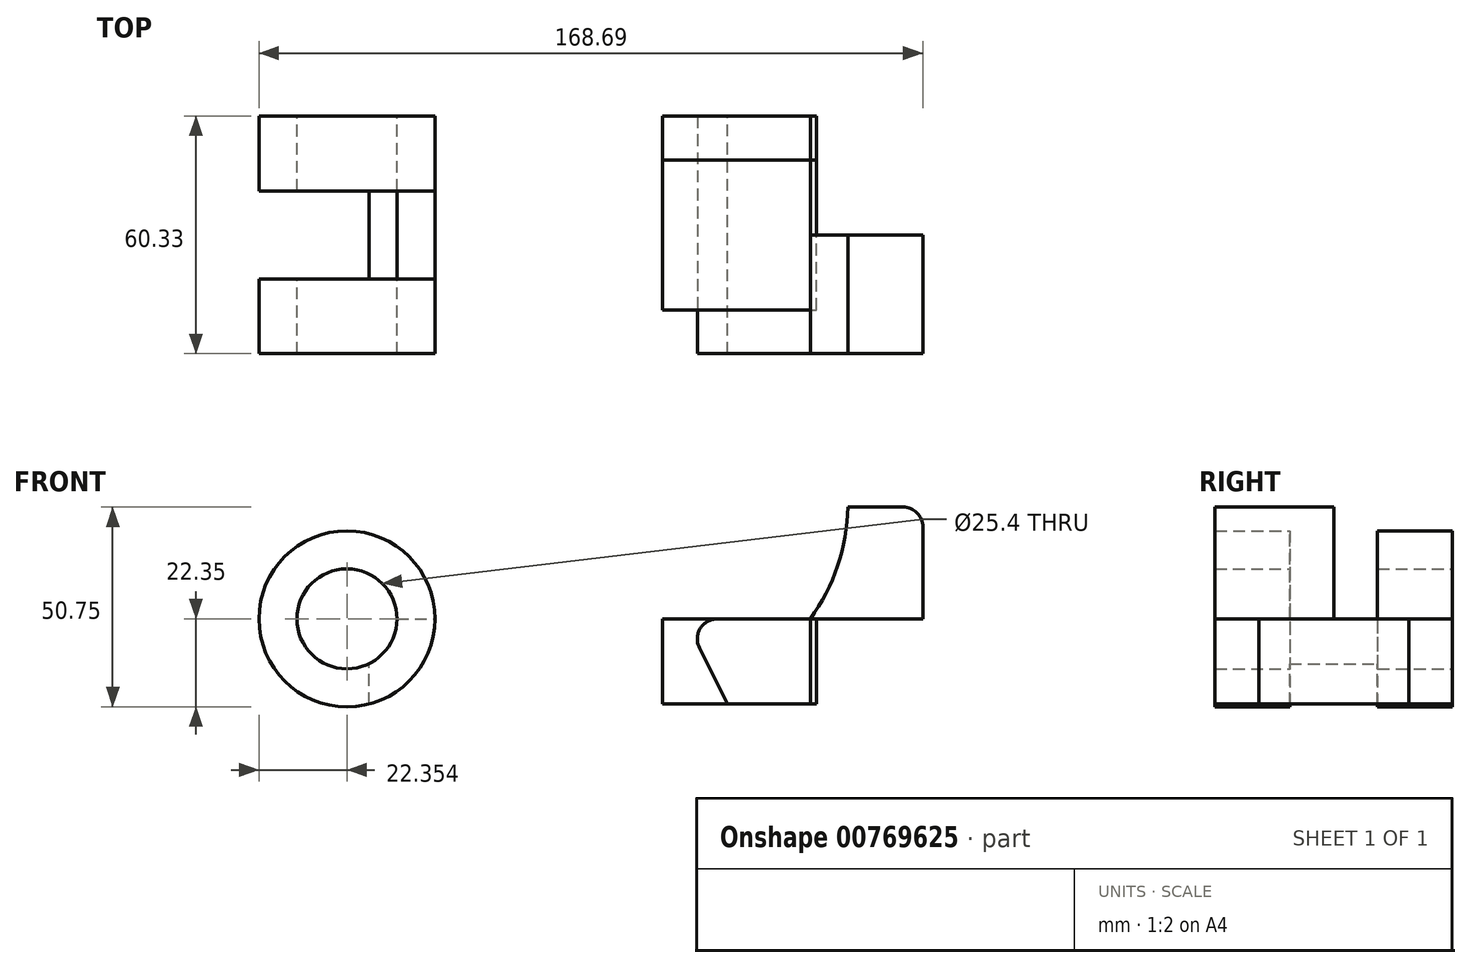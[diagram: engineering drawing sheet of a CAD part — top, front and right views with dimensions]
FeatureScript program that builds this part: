
annotation { "Feature Type Name" : "Feature", "Feature Type Description" : "" }
export const myFeature = defineFeature(function(context is Context, id is Id, definition is map)
    precondition{}
    {
        {
            var Q0;
            Q0=qCreatedBy(makeId("Front.planeOp"),FACE);
            var sketch = newSketch(context, id + "F0", { "sketchPlane" : qUnion([Q0])});
            skPoint(sketch, "E0.middle", {"position": v(114.94, 0) * mm});
            skCircle(sketch, "E1", {"center": v(12.24, 0) * mm, "radius": 12.7 * mm});
            skCircle(sketch, "E2", {"center": v(12.24, 0) * mm, "radius": 22.35 * mm});
            skPoint(sketch, "E3.orphan", {"position": v(17.84, -11.18) * mm});
            skPoint(sketch, "E0.bottom.end.orphan", {"position": v(6.65, 11.18) * mm});
            skPoint(sketch, "E0.left.end.orphan", {"position": v(223.24, -11.18) * mm});
            skPoint(sketch, "E0.left.start.orphan", {"position": v(212.05, 11.18) * mm});
            skLineSegment(sketch, "E4.bottom", {"start": v(108.99, -21.64) * mm, "end": v(200.14, -21.64) * mm});
            skLineSegment(sketch, "E4.top", {"start": v(17.84, 0) * mm, "end": v(200.14, 0) * mm});
            skLineSegment(sketch, "E4.left", {"start": v(17.84, -21.64) * mm, "end": v(17.84, 0) * mm});
            skLineSegment(sketch, "E4.right", {"start": v(200.14, -21.64) * mm, "end": v(200.14, 0) * mm});
            skLineSegment(sketch, "E5", {"start": v(12.24, 0) * mm, "end": v(98.1, 0) * mm});
            skLineSegment(sketch, "E6", {"start": v(17.84, -21.64) * mm, "end": v(130, -21.64) * mm});
            skLineSegment(sketch, "E7", {"start": v(17.84, -21.64) * mm, "end": v(108.99, -21.64) * mm});
            skLineSegment(sketch, "E8", {"start": v(98.1, 0) * mm, "end": v(108.99, -21.64) * mm});
            skLineSegment(sketch, "E9", {"start": v(130, -21.64) * mm, "end": v(130, 0) * mm});
            skLineSegment(sketch, "E10", {"start": v(139.53, 28.4) * mm, "end": v(158.58, 28.4) * mm});
            skLineSegment(sketch, "E11", {"start": v(158.58, 28.4) * mm, "end": v(158.58, 0) * mm});
            skLineSegment(sketch, "E12", {"start": v(114.94, 0) * mm, "end": v(114.94, 0) * mm});
            skLineSegment(sketch, "E13", {"start": v(114.94, 0) * mm, "end": v(130, 0) * mm});
            skLineSegment(sketch, "E14", {"start": v(114.94, 0) * mm, "end": v(98.1, 0) * mm});
            skPoint(sketch, "E15.end.orphan", {"position": v(120.48, 28.4) * mm});
            skPoint(sketch, "E16.third.point", {"position": v(121.98, 25.05) * mm});
            skPoint(sketch, "E17.orphan", {"position": v(140.3, 65.58) * mm});
            skPoint(sketch, "E18.trimOffspring.end.orphan", {"position": v(140.3, 0) * mm});
            skPoint(sketch, "E16.center.orphan", {"position": v(133.04, 14.78) * mm});
            skPoint(sketch, "E19.third.point", {"position": v(62.85, 73.34) * mm});
            skArc(sketch, "E20.trimOffspring", {"start": v(130, 0) * mm, "mid": v(136.9, 13.48) * mm, "end": v(139.53, 28.4) * mm});
            skSolve(sketch);
        }
        {
            var Q0;
            {var subQ0=sQuery(id+"F0.wireOp",EDGE,"E7");Q0=makeQuery(id+"F0.imprint","IMPRINT",FACE,{"disambiguationData":[TD([[makeQuery(id+"F0.imprint","IMPRINT",EDGE,{"derivedFrom":subQ0}),1.0]])]});}
            var Q1;
            Q1=makeQuery(id+"F0.imprint","IMPRINT",FACE,{"disambiguationData":[TD([[makeQuery(id+"F0.imprint","IMPRINT",EDGE,{"derivedFrom":sQuery(id+"F0.wireOp",EDGE,"E4.bottom")}),1.0]])]});
            var Q2;
            {var subQ0=sQuery(id+"F0.wireOp",EDGE,"E15");Q2=makeQuery(id+"F0.imprint","IMPRINT",FACE,{"disambiguationData":[TD([[makeQuery(id+"F0.imprint","IMPRINT",EDGE,{"derivedFrom":subQ0}),-1.0]])]});}
            var Q3;
            {var subQ0=sQuery(id+"F0.wireOp",EDGE,"E4.left");var subQ1=sQuery(id+"F0.wireOp",EDGE,"E1");var subQ2=makeQuery(id+"F0.imprint","INTERSECT",VERTEX,{"derivedFrom":[subQ1,subQ0]});Q3=makeQuery(id+"F0.imprint","IMPRINT",FACE,{"disambiguationData":[TD([[makeQuery(id+"F0.imprint","IMPRINT",EDGE,{"disambiguationData":[TD([[subQ2,-1.0]])],"derivedFrom":subQ1}),-1.0]])]});}
            var Q4;
            {var subQ0=sQuery(id+"F0.wireOp",EDGE,"E4.left");var subQ1=sQuery(id+"F0.wireOp",EDGE,"E1");var subQ2=makeQuery(id+"F0.imprint","INTERSECT",VERTEX,{"derivedFrom":[subQ1,subQ0]});Q4=makeQuery(id+"F0.imprint","IMPRINT",FACE,{"disambiguationData":[TD([[makeQuery(id+"F0.imprint","IMPRINT",EDGE,{"disambiguationData":[TD([[subQ2,1.0]])],"derivedFrom":subQ1}),-1.0]])]});}
            extrude(context, id + "F1", {"entities" : qUnion([Q0, Q1, Q2, Q3, Q4]), "endBound" : BoundingType.SYMMETRIC, "depth" : 60.32 * mm, "offsetDistance" : 25.4 * mm});
        }
        {
            var Q0;
            Q0=qCreatedBy(makeId("Front.planeOp"),FACE);
            var sketch = newSketch(context, id + "F2", { "sketchPlane" : qUnion([Q0])});
            skLineSegment(sketch, "E21.bottom", {"start": v(92.41, 0) * mm, "end": v(131.5, 0) * mm});
            skLineSegment(sketch, "E21.left", {"start": v(92.41, 0) * mm, "end": v(92.41, 0) * mm});
            skPoint(sketch, "E21.middle", {"position": v(131.5, 0) * mm});
            skLineSegment(sketch, "E22", {"start": v(131.5, 0) * mm, "end": v(131.5, 0) * mm});
            skPoint(sketch, "E21.right.end.orphan", {"position": v(170.6, 0) * mm});
            skPoint(sketch, "E21.right.start.orphan", {"position": v(170.6, 0) * mm});
            skLineSegment(sketch, "E23", {"start": v(92.41, 0) * mm, "end": v(92.41, -21.64) * mm});
            skLineSegment(sketch, "E24", {"start": v(92.41, -21.64) * mm, "end": v(131.5, -21.64) * mm});
            skLineSegment(sketch, "E25", {"start": v(134, -21.64) * mm, "end": v(131.5, -21.64) * mm});
            skLineSegment(sketch, "E26", {"start": v(131.5, -21.64) * mm, "end": v(131.5, 0) * mm});
            skSolve(sketch);
        }
        {
            var Q0;
            {var subQ1=sQuery(id+"F2.wireOp",EDGE,"E22");Q0=makeQuery(id+"F2.imprint","IMPRINT",FACE,{"disambiguationData":[TD([[makeQuery(id+"F2.imprint","IMPRINT",EDGE,{"derivedFrom":subQ1}),-1.0]])]});}
            extrude(context, id + "F3", {"entities" : qUnion([Q0]), "endBound" : BoundingType.SYMMETRIC, "depth" : 38.1 * mm, "offsetDistance" : 25.4 * mm});
        }
        {
            var Q0;
            Q0=makeQuery(id+"F1.opExtrude","SWEPT_EDGE",EDGE,{"disambiguationData":[OSD([sQuery(id+"F0.wireOp",EDGE,"E4.top"),sQuery(id+"F0.wireOp",EDGE,"E4.right")])]});
            var Q1;
            Q1=makeQuery(id+"F1.opExtrude","SWEPT_EDGE",EDGE,{"disambiguationData":[OSD([sQuery(id+"F0.wireOp",EDGE,"E4.top"),sQuery(id+"F0.wireOp",EDGE,"E11")])]});
            var Q2;
            Q2=makeQuery(id+"F1.opExtrude","SWEPT_EDGE",EDGE,{"disambiguationData":[OSD([sQuery(id+"F0.wireOp",EDGE,"E10"),sQuery(id+"F0.wireOp",EDGE,"E11")])]});
            fillet(context, id + "F4", {"entities" : qUnion([Q0, Q1, Q2]), "radius" : 5.08 * mm, "tangentPropagation" : true, "allowEdgeOverflow" : false});
        }
        {
            var Q0;
            {var subQ0=sQuery(id+"F0.wireOp",EDGE,"U9p8KZc0-DV8N-GcPJ-SEQa-MMcg6suNOH3D");Q0=makeQuery(id+"F0.imprint","IMPRINT",FACE,{"disambiguationData":[TD([[makeQuery(id+"F0.imprint","IMPRINT",EDGE,{"derivedFrom":subQ0}),-1.0]])]});}
            var Q1;
            Q1=makeQuery(id+"F0.imprint","IMPRINT",FACE,{"disambiguationData":[TD([[makeQuery(id+"F0.imprint","IMPRINT",EDGE,{"derivedFrom":sQuery(id+"F0.wireOp",EDGE,"E10")}),-1.0]])]});
            extrude(context, id + "F5", {"entities" : qUnion([Q0, Q1]), "depth" : 30.1 * mm, "offsetDistance" : 25.4 * mm});
        }
        {
            var Q0;
            Q0=makeQuery(id+"F5.opExtrude","SWEPT_EDGE",EDGE,{"disambiguationData":[OSD([sQuery(id+"F0.wireOp",EDGE,"E10"),sQuery(id+"F0.wireOp",EDGE,"E11")])]});
            fillet(context, id + "F6", {"entities" : qUnion([Q0]), "radius" : 5.08 * mm, "allowEdgeOverflow" : false});
        }
        {
            var Q0;
            Q0=makeQuery(id+"F3.opExtrude","CAP_FACE",FACE,{"disambiguationData":[OSD([sQuery(id+"F2.wireOp",EDGE,"E21.bottom"),sQuery(id+"F2.wireOp",EDGE,"E22"),sQuery(id+"F2.wireOp",EDGE,"E23"),sQuery(id+"F2.wireOp",EDGE,"E24"),sQuery(id+"F2.wireOp",EDGE,"E26")])],"isStart":true});
            extrude(context, id + "F7", {"entities" : qUnion([Q0]), "depth" : 11.12 * mm, "offsetDistance" : 25.4 * mm});
        }
        {
            var Q0;
            {var subQ0=sQuery(id+"F0.wireOp",EDGE,"E4.left");var subQ1=sQuery(id+"F0.wireOp",EDGE,"E1");var subQ2=makeQuery(id+"F0.imprint","INTERSECT",VERTEX,{"derivedFrom":[subQ1,subQ0]});Q0=makeQuery(id+"F0.imprint","IMPRINT",FACE,{"disambiguationData":[TD([[makeQuery(id+"F0.imprint","IMPRINT",EDGE,{"disambiguationData":[TD([[subQ2,1.0]])],"derivedFrom":subQ1}),-1.0]])]});}
            var Q1;
            Q1=sQuery(id+"F0.wireOp",EDGE,"E2");
            extrude(context, id + "F8", {"entities" : qUnion([Q0]), "operationType" : NewBodyOperationType.REMOVE, "surfaceEntities" : qUnion([Q1]), "endBound" : BoundingType.SYMMETRIC, "depth" : 22.33 * mm, "offsetDistance" : 25.4 * mm});
        }
    });
